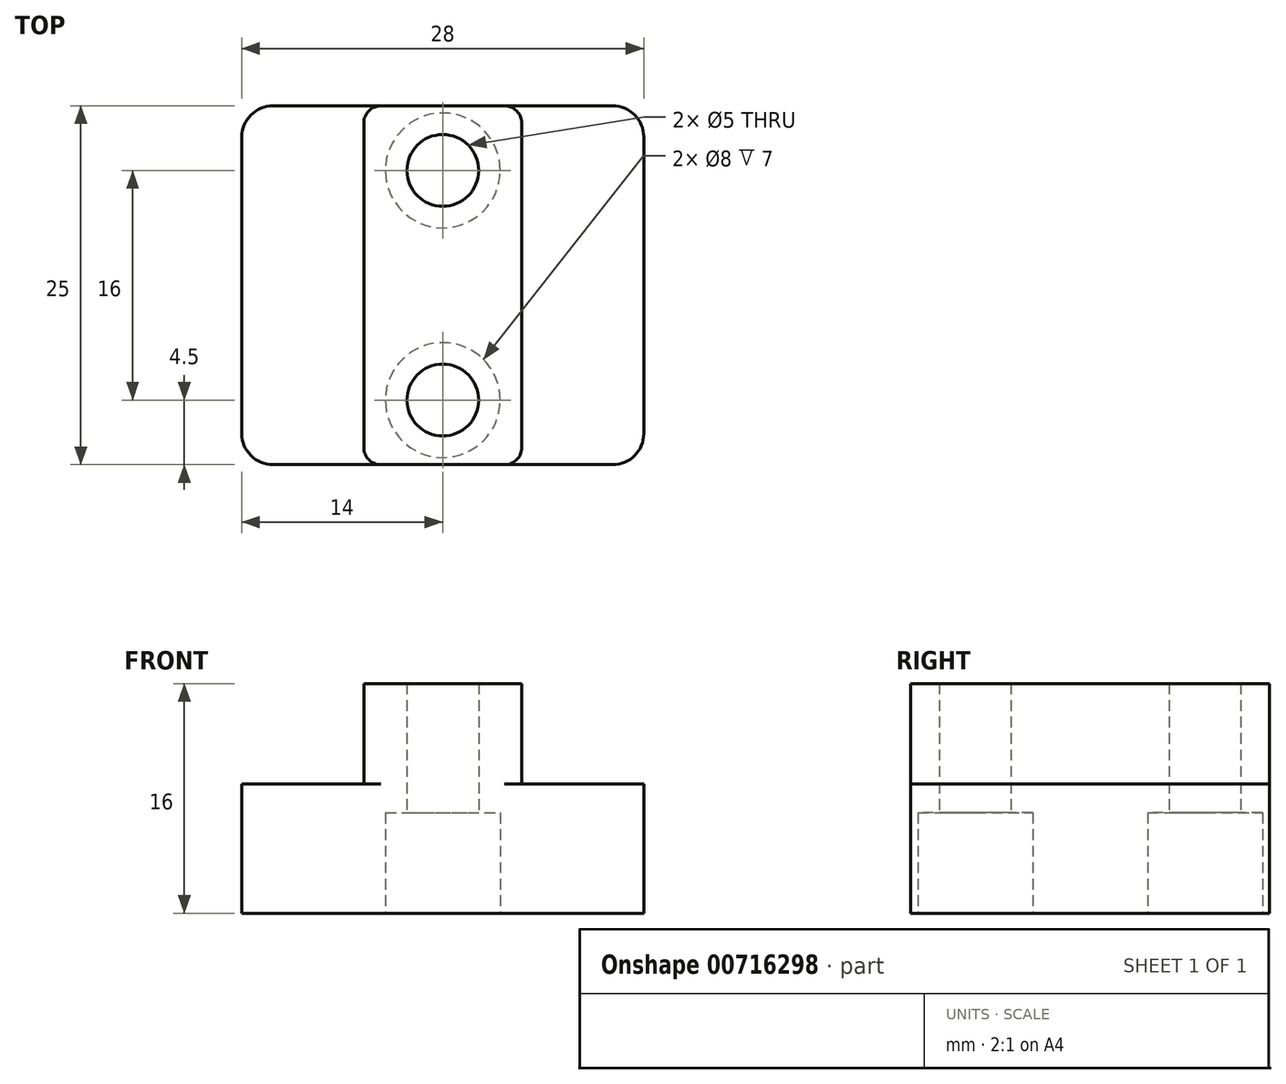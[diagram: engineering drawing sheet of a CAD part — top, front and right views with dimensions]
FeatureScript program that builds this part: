
annotation { "Feature Type Name" : "Feature", "Feature Type Description" : "" }
export const myFeature = defineFeature(function(context is Context, id is Id, definition is map)
    precondition{}
    {
        {
            var Q0;
            Q0=qCreatedBy(makeId("Front.planeOp"),FACE);
            var sketch = newSketch(context, id + "F0", { "sketchPlane" : qUnion([Q0])});
            skLineSegment(sketch, "E0.bottom", {"start": v(14, 8) * mm, "end": v(-14, 8) * mm});
            skLineSegment(sketch, "E0.top", {"start": v(14, -8) * mm, "end": v(-14, -8) * mm});
            skLineSegment(sketch, "E0.left", {"start": v(14, 8) * mm, "end": v(14, -8) * mm});
            skLineSegment(sketch, "E0.right", {"start": v(-14, 8) * mm, "end": v(-14, -8) * mm});
            skPoint(sketch, "E0.middle", {"position": v(0, 0) * mm});
            skLineSegment(sketch, "E1.bottom", {"start": v(6, 8) * mm, "end": v(-6, 8) * mm});
            skLineSegment(sketch, "E2.bottom", {"start": v(14, 8) * mm, "end": v(6, 8) * mm});
            skLineSegment(sketch, "E2.left", {"start": v(14, 8) * mm, "end": v(14, 1) * mm});
            skLineSegment(sketch, "E3.bottom", {"start": v(-14, 8) * mm, "end": v(-6, 8) * mm});
            skLineSegment(sketch, "E3.left", {"start": v(-14, 8) * mm, "end": v(-14, 1) * mm});
            skLineSegment(sketch, "E4.bottom", {"start": v(5.5, 1) * mm, "end": v(-5.5, 1) * mm});
            skLineSegment(sketch, "E4.top", {"start": v(5.5, 8) * mm, "end": v(-5.5, 8) * mm});
            skLineSegment(sketch, "E4.left", {"start": v(5.5, 1) * mm, "end": v(5.5, 8) * mm});
            skLineSegment(sketch, "E4.right", {"start": v(-5.5, 1) * mm, "end": v(-5.5, 8) * mm});
            skPoint(sketch, "E4.middle", {"position": v(0, 4.5) * mm});
            skPoint(sketch, "E4.middle.positionSnap0", {"position": v(6, 4.5) * mm});
            skPoint(sketch, "E4.centerSnap0", {"position": v(6, 4.5) * mm});
            skLineSegment(sketch, "E5", {"start": v(5.5, 1) * mm, "end": v(14, 1) * mm});
            skLineSegment(sketch, "E6", {"start": v(-5.5, 1) * mm, "end": v(-14, 1) * mm});
            skSolve(sketch);
        }
        {
            var Q0;
            Q0=makeQuery(id+"F0.imprint","IMPRINT",FACE,{"disambiguationData":[TD([[makeQuery(id+"F0.imprint","IMPRINT",EDGE,{"derivedFrom":sQuery(id+"F0.wireOp",EDGE,"E0.top")}),-1.0]])]});
            var Q1;
            Q1=makeQuery(id+"F0.imprint","IMPRINT",FACE,{"disambiguationData":[TD([[makeQuery(id+"F0.imprint","IMPRINT",EDGE,{"derivedFrom":sQuery(id+"F0.wireOp",EDGE,"E4.bottom")}),-1.0]])]});
            extrude(context, id + "F1", {"entities" : qUnion([Q0, Q1]), "endBound" : BoundingType.SYMMETRIC, "depth" : 25 * mm, "offsetDistance" : 25 * mm});
        }
        {
            var Q0;
            Q0=makeQuery(id+"F1.opExtrude","SWEPT_FACE",FACE,{"disambiguationData":[OSD([sQuery(id+"F0.wireOp",EDGE,"E0.top")])]});
            var sketch = newSketch(context, id + "F2", { "sketchPlane" : qUnion([Q0])});
            skLineSegment(sketch, "E7.bottom", {"start": v(0, 8) * mm, "end": v(0, 8) * mm});
            skLineSegment(sketch, "E7.top", {"start": v(0, -8) * mm, "end": v(0, -8) * mm});
            skLineSegment(sketch, "E7.left", {"start": v(0, 8) * mm, "end": v(0, -8) * mm});
            skLineSegment(sketch, "E7.right", {"start": v(0, 8) * mm, "end": v(0, -8) * mm});
            skPoint(sketch, "E7.middle", {"position": v(0, 0) * mm});
            skCircle(sketch, "E8", {"center": v(0, 8) * mm, "radius": 4 * mm});
            skCircle(sketch, "E9", {"center": v(0, -8) * mm, "radius": 4 * mm});
            skCircle(sketch, "E10", {"center": v(0, 8) * mm, "radius": 2.5 * mm});
            skCircle(sketch, "E11", {"center": v(0, -8) * mm, "radius": 2.5 * mm});
            skSolve(sketch);
        }
        {
            var Q0;
            Q0=makeQuery(id+"F2.imprint","IMPRINT",FACE,{"disambiguationData":[TD([[makeQuery(id+"F2.imprint","IMPRINT",EDGE,{"derivedFrom":sQuery(id+"F2.wireOp",EDGE,"E10")}),1.0]])]});
            var Q1;
            Q1=makeQuery(id+"F2.imprint","IMPRINT",FACE,{"disambiguationData":[TD([[makeQuery(id+"F2.imprint","IMPRINT",EDGE,{"derivedFrom":sQuery(id+"F2.wireOp",EDGE,"E11")}),1.0]])]});
            extrude(context, id + "F3", {"entities" : qUnion([Q0, Q1]), "operationType" : NewBodyOperationType.REMOVE, "oppositeDirection" : true, "depth" : 25 * mm, "offsetDistance" : 25 * mm});
        }
        {
            var Q0;
            Q0=makeQuery(id+"F2.imprint","IMPRINT",FACE,{"disambiguationData":[TD([[makeQuery(id+"F2.imprint","IMPRINT",EDGE,{"derivedFrom":sQuery(id+"F2.wireOp",EDGE,"E8")}),1.0]])]});
            var Q1;
            Q1=makeQuery(id+"F2.imprint","IMPRINT",FACE,{"disambiguationData":[TD([[makeQuery(id+"F2.imprint","IMPRINT",EDGE,{"derivedFrom":sQuery(id+"F2.wireOp",EDGE,"E9")}),1.0]])]});
            extrude(context, id + "F4", {"entities" : qUnion([Q0, Q1]), "operationType" : NewBodyOperationType.REMOVE, "oppositeDirection" : true, "depth" : 7 * mm, "offsetDistance" : 25 * mm});
        }
        {
            var Q0;
            Q0=makeQuery(id+"F1.opExtrude","CAP_EDGE",EDGE,{"disambiguationData":[OSD([sQuery(id+"F0.wireOp",EDGE,"E0.right")])],"isStart":false});
            var Q1;
            Q1=makeQuery(id+"F1.opExtrude","CAP_EDGE",EDGE,{"disambiguationData":[OSD([sQuery(id+"F0.wireOp",EDGE,"E0.left")])],"isStart":false});
            var Q2;
            Q2=makeQuery(id+"F1.opExtrude","CAP_EDGE",EDGE,{"disambiguationData":[OSD([sQuery(id+"F0.wireOp",EDGE,"E0.left")])],"isStart":true});
            var Q3;
            Q3=makeQuery(id+"F1.opExtrude","CAP_EDGE",EDGE,{"disambiguationData":[OSD([sQuery(id+"F0.wireOp",EDGE,"E0.right")])],"isStart":true});
            fillet(context, id + "F5", {"entities" : qUnion([Q0, Q1, Q2, Q3]), "radius" : 2.17 * mm, "tangentPropagation" : true, "allowEdgeOverflow" : false});
        }
        {
            var Q0;
            Q0=makeQuery(id+"F1.opExtrude","CAP_EDGE",EDGE,{"disambiguationData":[OSD([sQuery(id+"F0.wireOp",EDGE,"E4.left")])],"isStart":false});
            var Q1;
            Q1=makeQuery(id+"F1.opExtrude","CAP_EDGE",EDGE,{"disambiguationData":[OSD([sQuery(id+"F0.wireOp",EDGE,"E4.right")])],"isStart":false});
            var Q2;
            Q2=makeQuery(id+"F1.opExtrude","CAP_EDGE",EDGE,{"disambiguationData":[OSD([sQuery(id+"F0.wireOp",EDGE,"E4.left")])],"isStart":true});
            var Q3;
            Q3=makeQuery(id+"F1.opExtrude","CAP_EDGE",EDGE,{"disambiguationData":[OSD([sQuery(id+"F0.wireOp",EDGE,"E4.right")])],"isStart":true});
            fillet(context, id + "F6", {"entities" : qUnion([Q0, Q1, Q2, Q3]), "radius" : 1.2 * mm, "tangentPropagation" : true, "allowEdgeOverflow" : false});
        }
    });
